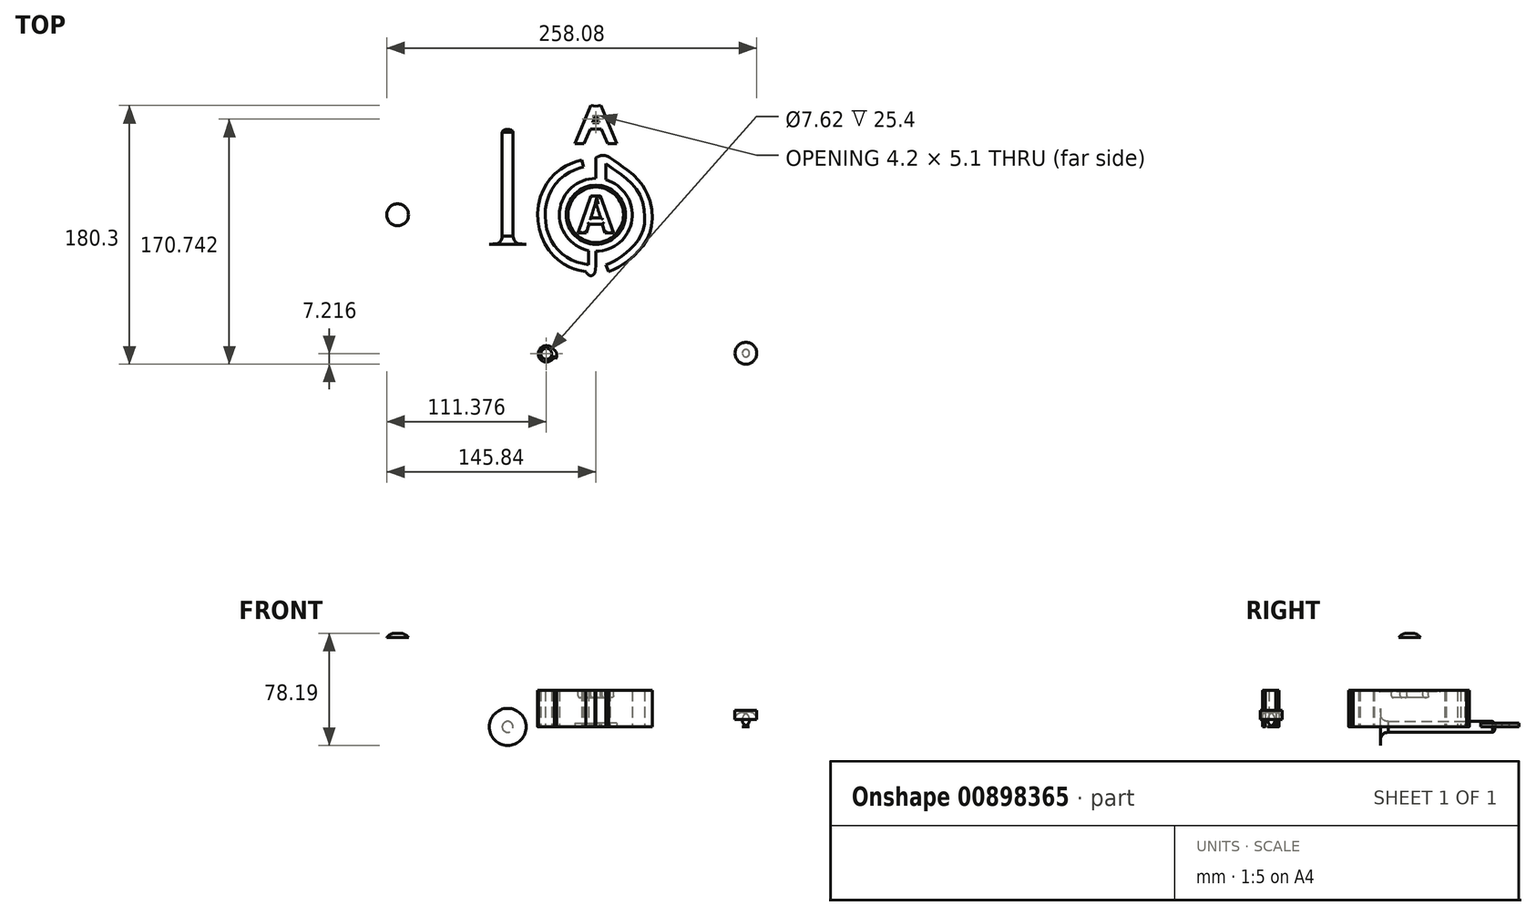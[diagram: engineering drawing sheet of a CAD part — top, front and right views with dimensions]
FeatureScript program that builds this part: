
annotation { "Feature Type Name" : "Feature", "Feature Type Description" : "" }
export const myFeature = defineFeature(function(context is Context, id is Id, definition is map)
    precondition{}
    {
        {
            var Q0;
            Q0=qCreatedBy(makeId("Top.planeOp"),FACE);
            var sketch = newSketch(context, id + "F0", { "sketchPlane" : qUnion([Q0])});
            skCircle(sketch, "E0", {"center": v(0, 0) * mm, "radius": 25.4 * mm});
            skLineSegment(sketch, "E1", {"start": v(0, 25.4) * mm, "end": v(0, 35.55) * mm});
            skLineSegment(sketch, "E2", {"start": v(0, -25.4) * mm, "end": v(0, -35.56) * mm});
            skFitSpline(sketch, "E3", {"points": [v(0, -35.56) * mm, v(-14.55, -32.5) * mm, v(-25.05, -25.72) * mm, v(-32.63, -14.55) * mm, v(-35.29, 2.2) * mm, v(-29.44, 19.74) * mm, v(-18, 29.84) * mm, v(-8.44, 33.43) * mm], "startDerivative": vector(-105, 14.53) * mm, "endDerivative": vector(78.17, 22.79) * mm});
            skFitSpline(sketch, "E4.0", {"points": [v(-0.7, -40.6) * mm, v(-1.8, -40.44) * mm, v(-4, -40.13) * mm, v(-7.4, -39.6) * mm, v(-10.23, -39.04) * mm, v(-12.5, -38.48) * mm, v(-14.2, -38) * mm, v(-15.6, -37.53) * mm, v(-16.7, -37.11) * mm, v(-18.35, -36.45) * mm, v(-20.72, -35.3) * mm, v(-23.66, -33.5) * mm, v(-25.92, -31.77) * mm, v(-27.63, -30.29) * mm, v(-29.26, -28.73) * mm, v(-31.2, -26.64) * mm, v(-33.34, -23.88) * mm, v(-35.25, -20.87) * mm, v(-36.9, -17.62) * mm, v(-38.28, -14.12) * mm, v(-39.34, -10.44) * mm, v(-40.07, -6.6) * mm, v(-40.46, -2.64) * mm, v(-40.48, 1.41) * mm, v(-40.11, 5.51) * mm, v(-39.35, 9.58) * mm, v(-38.2, 13.57) * mm, v(-36.65, 17.43) * mm, v(-35.2, 20.17) * mm, v(-34.1, 21.92) * mm, v(-33.32, 23.07) * mm, v(-31.9, 24.99) * mm, v(-29.68, 27.48) * mm, v(-26.83, 30.08) * mm, v(-24.35, 31.93) * mm, v(-22.35, 33.22) * mm, v(-20.85, 34.09) * mm, v(-19.36, 34.87) * mm, v(-17.4, 35.78) * mm, v(-15.04, 36.7) * mm, v(-12.36, 37.58) * mm, v(-10.68, 38.07) * mm, v(-9.86, 38.3) * mm]});
            skLineSegment(sketch, "E5", {"start": v(-0.7, -40.6) * mm, "end": v(0, -35.56) * mm});
            skLineSegment(sketch, "E6", {"start": v(-9.86, 38.3) * mm, "end": v(-8.44, 33.43) * mm});
            skLineSegment(sketch, "E7", {"start": v(-5.08, -34.86) * mm, "end": v(-5.08, -24.89) * mm});
            skFitSpline(sketch, "E8", {"points": [v(7.04, 35.55) * mm, v(14.69, 30.24) * mm, v(29.7, 15.62) * mm, v(33.56, -8.04) * mm, v(26.12, -21.73) * mm, v(14.42, -31.3) * mm, v(7.04, -34.76) * mm], "startDerivative": vector(51.9, -35.75) * mm, "endDerivative": vector(-56.85, -22.28) * mm});
            skFitSpline(sketch, "E9.0", {"points": [v(9.92, 39.74) * mm, v(10.46, 39.36) * mm, v(11.54, 38.62) * mm, v(13.24, 37.44) * mm, v(14.77, 36.38) * mm, v(16.1, 35.46) * mm, v(17.15, 34.72) * mm, v(18.26, 33.93) * mm, v(19.48, 33.07) * mm, v(20.76, 32.14) * mm, v(22.54, 30.8) * mm, v(24.86, 28.93) * mm, v(27.68, 26.37) * mm, v(29.97, 23.93) * mm, v(31.7, 21.78) * mm, v(32.73, 20.35) * mm, v(33.51, 19.15) * mm, v(34.07, 18.23) * mm, v(34.6, 17.27) * mm, v(35.27, 15.99) * mm, v(36.02, 14.34) * mm, v(37.06, 11.66) * mm, v(38.07, 8.22) * mm, v(38.85, 4.05) * mm, v(39.23, -0.1) * mm, v(39.2, -4.15) * mm, v(38.86, -7.4) * mm, v(38.38, -9.9) * mm, v(37.77, -12.29) * mm, v(36.76, -15.1) * mm, v(35.21, -18.17) * mm, v(33.4, -20.98) * mm, v(31.7, -23.1) * mm, v(30.28, -24.72) * mm, v(28.81, -26.28) * mm, v(26.88, -28.17) * mm, v(24.48, -30.3) * mm, v(22.02, -32.27) * mm, v(19.98, -33.75) * mm, v(18.37, -34.83) * mm, v(17.18, -35.58) * mm, v(16, -36.26) * mm, v(14.5, -37.07) * mm, v(12.7, -37.93) * mm, v(10.71, -38.77) * mm, v(9.48, -39.25) * mm, v(8.9, -39.49) * mm]});
            skLineSegment(sketch, "E10", {"start": v(0, 39.74) * mm, "end": v(0, 35.55) * mm});
            skLineSegment(sketch, "E11", {"start": v(7.04, 35.55) * mm, "end": v(7.04, 24.4) * mm});
            skLineSegment(sketch, "E12", {"start": v(7.04, -34.76) * mm, "end": v(8.9, -39.49) * mm});
            skFitSpline(sketch, "E13", {"points": [v(9.92, 39.74) * mm, v(6.86, 41.24) * mm, v(3.27, 41.24) * mm, v(0, 39.74) * mm], "startDerivative": vector(-8.92, 5.5) * mm, "endDerivative": vector(-9.37, -5.34) * mm});
            skPoint(sketch, "E14.endDerivative.orphan", {"position": v(6.86, 42.74) * mm});
            skPoint(sketch, "E14.startDerivative.orphan", {"position": v(8.4, 41.24) * mm});
            skPoint(sketch, "E15.1.internal.orphan", {"position": v(-2.62, -40.6) * mm});
            skFitSpline(sketch, "E16", {"points": [v(-0.7, -40.6) * mm, v(-2.62, -42.28) * mm, v(-4.27, -42.28) * mm, v(-6.26, -40.6) * mm, v(-7.03, -39.64) * mm], "startDerivative": vector(-6.65, -7.21) * mm, "endDerivative": vector(-3.2, 4.38) * mm});
            skPoint(sketch, "E17.orphan", {"position": v(4, 0) * mm});
            skPoint(sketch, "E18", {"position": v(0, -3.17) * mm});
            skPoint(sketch, "E19.start.orphan", {"position": v(-10.06, 0) * mm});
            skCircle(sketch, "E20", {"center": v(0, 0) * mm, "radius": 19.32 * mm});
            skCircle(sketch, "E21", {"center": v(0, 0) * mm, "radius": 20.67 * mm});
            skCircle(sketch, "E22", {"center": v(-34.46, -96.85) * mm, "radius": 3.81 * mm});
            skArc(sketch, "E23", {"start": v(-29.9, -93.5) * mm, "mid": v(-40.02, -98.01) * mm, "end": v(-28.93, -98.1) * mm});
            skLineSegment(sketch, "E24", {"start": v(-28.93, -98.1) * mm, "end": v(-27.97, -100.51) * mm});
            skArc(sketch, "E25", {"start": v(-27.97, -100.51) * mm, "mid": v(-27.37, -96.57) * mm, "end": v(-29.9, -93.5) * mm});
            skPoint(sketch, "E26.end.orphan", {"position": v(9.26, -7.36) * mm});
            skPoint(sketch, "E27.end.orphan", {"position": v(-17.78, -7.36) * mm});
            skPoint(sketch, "E27.start.orphan", {"position": v(0, 12.15) * mm});
            skPoint(sketch, "E28.start.orphan", {"position": v(0, 4.35) * mm});
            skPoint(sketch, "E29.start.orphan", {"position": v(-3.86, 0) * mm});
            skSolve(sketch);
        }
        {
            var Q0;
            Q0 = qSketchRegion(id + "F0", true);
            extrude(context, id + "F1", {"entities" : qUnion([Q0]), "depth" : 25.4 * mm, "offsetDistance" : 25.4 * mm});
        }
        {
            var Q0;
            Q0=qCreatedBy(makeId("Front.planeOp"),FACE);
            var sketch = newSketch(context, id + "F2", { "sketchPlane" : qUnion([Q0])});
            skLineSegment(sketch, "E30", {"start": v(-130.6, 62.22) * mm, "end": v(-138.22, 62.22) * mm});
            skFitSpline(sketch, "E31", {"points": [v(-130.6, 62.22) * mm, v(-131.95, 63.64) * mm, v(-133.54, 64.67) * mm, v(-135.8, 65.24) * mm, v(-138.22, 65.25) * mm], "startDerivative": vector(-4.63, 6.31) * mm, "endDerivative": vector(-8.46, -0.46) * mm});
            skLineSegment(sketch, "E32", {"start": v(-138.22, 65.25) * mm, "end": v(-138.22, 62.22) * mm});
            skSolve(sketch);
        }
        {
            var Q0;
            Q0=makeQuery(id+"F0.imprint","IMPRINT",FACE,{"disambiguationData":[TD([[makeQuery(id+"F0.imprint","IMPRINT",EDGE,{"derivedFrom":sQuery(id+"F0.wireOp",EDGE,"E20")}),-1.0]])]});
            var Q1;
            Q1=makeQuery(id+"F0.imprint","IMPRINT",FACE,{"disambiguationData":[TD([[makeQuery(id+"F0.imprint","IMPRINT",EDGE,{"derivedFrom":sQuery(id+"F0.wireOp",EDGE,"E28")}),-1.0]])]});
            extrude(context, id + "F3", {"entities" : qUnion([Q0, Q1]), "operationType" : NewBodyOperationType.ADD, "depth" : 24.9 * mm, "offsetDistance" : 25.4 * mm});
        }
        {
            var Q0;
            Q0=makeQuery(id+"F2.imprint","IMPRINT",FACE,{"disambiguationData":[TD([[makeQuery(id+"F2.imprint","IMPRINT",EDGE,{"derivedFrom":sQuery(id+"F2.wireOp",EDGE,"E30")}),-1.0]])]});
            var Q1;
            Q1=sQuery(id+"F2.wireOp",EDGE,"E32");
            revolve(context, id + "F4", {"surfaceOperationType" : NewSurfaceOperationType.NEW, "entities" : qUnion([Q0]), "axis" : qUnion([Q1]), "revolveType" : RevolveType.FULL});
        }
        {
            var Q0;
            Q0=qCreatedBy(makeId("Top.planeOp"),FACE);
            var sketch = newSketch(context, id + "F5", { "sketchPlane" : qUnion([Q0])});
            skLineSegment(sketch, "E33.top", {"start": v(-65.27, 27.3) * mm, "end": v(-61.46, 27.3) * mm});
            skLineSegment(sketch, "E33.left", {"start": v(-65.27, 57.66) * mm, "end": v(-65.27, 27.3) * mm});
            skLineSegment(sketch, "E33.right", {"start": v(-61.46, 57.66) * mm, "end": v(-61.46, 27.3) * mm});
            skFitSpline(sketch, "E34", {"points": [v(-65.27, 57.66) * mm, v(-64.7, 58.62) * mm, v(-63.78, 59.15) * mm, v(-62.33, 59.48) * mm, v(-61.46, 59.55) * mm], "startDerivative": vector(2.04, 4.24) * mm, "endDerivative": vector(3.67, 0.16) * mm});
            skLineSegment(sketch, "E35", {"start": v(-61.46, 59.55) * mm, "end": v(-61.46, 57.66) * mm});
            skLineSegment(sketch, "E36", {"start": v(-65.27, 27.3) * mm, "end": v(-65.27, 15.9) * mm});
            skLineSegment(sketch, "E37", {"start": v(-61.46, 27.3) * mm, "end": v(-61.46, 15.9) * mm});
            skLineSegment(sketch, "E38", {"start": v(-61.46, 15.9) * mm, "end": v(-65.27, 15.9) * mm});
            skLineSegment(sketch, "E39", {"start": v(-61.46, 15.9) * mm, "end": v(-61.46, -14.88) * mm});
            skLineSegment(sketch, "E40", {"start": v(-65.27, -14.88) * mm, "end": v(-65.27, 15.9) * mm});
            skFitSpline(sketch, "E41", {"points": [v(-65.27, -14.88) * mm, v(-65.92, -17.73) * mm, v(-68.2, -19.87) * mm, v(-71.2, -20.38) * mm, v(-74.37, -20.47) * mm], "startDerivative": vector(-1.14, -12.1) * mm, "endDerivative": vector(-12.5, -0.3) * mm});
            skLineSegment(sketch, "E42", {"start": v(-74.37, -20.47) * mm, "end": v(-61.46, -20.47) * mm});
            skLineSegment(sketch, "E43", {"start": v(-61.46, -20.47) * mm, "end": v(-61.46, -14.88) * mm});
            skSolve(sketch);
        }
        {
            var Q0;
            Q0 = qSketchRegion(id + "F5", true);
            var Q1;
            Q1=sQuery(id+"F5.wireOp",EDGE,"E33.right");
            revolve(context, id + "F6", {"surfaceOperationType" : NewSurfaceOperationType.NEW, "entities" : qUnion([Q0]), "axis" : qUnion([Q1]), "revolveType" : RevolveType.FULL});
        }
        {
            var Q0;
            Q0=qCreatedBy(makeId("Top.planeOp"),FACE);
            var sketch = newSketch(context, id + "F7", { "sketchPlane" : qUnion([Q0])});
            skCircle(sketch, "E44", {"center": v(104.62, -96.45) * mm, "radius": 7.62 * mm});
            skPoint(sketch, "E45.center.orphan", {"position": v(104.62, 20.59) * mm});
            skSolve(sketch);
        }
        {
            var Q0;
            Q0 = qSketchRegion(id + "F7", true);
            extrude(context, id + "F8", {"entities" : qUnion([Q0]), "depth" : 11.43 * mm, "offsetDistance" : 25.4 * mm});
        }
        {
            var Q0;
            Q0=makeQuery(id+"F8.opExtrude","CAP_EDGE",EDGE,{"disambiguationData":[OSD([sQuery(id+"F7.wireOp",EDGE,"E44")])],"isStart":true});
            fillet(context, id + "F9", {"entities" : qUnion([Q0]), "radius" : 5.08 * mm, "tangentPropagation" : true, "allowEdgeOverflow" : false});
        }
        {
            var Q0;
            Q0=makeQuery(id+"F0.imprint","IMPRINT",FACE,{"disambiguationData":[TD([[makeQuery(id+"F0.imprint","IMPRINT",EDGE,{"derivedFrom":sQuery(id+"F0.wireOp",EDGE,"E20")}),1.0]])]});
            extrude(context, id + "F10", {"entities" : qUnion([Q0]), "operationType" : NewBodyOperationType.ADD, "depth" : 25.4 * mm, "offsetDistance" : 25.4 * mm});
        }
        {
            var Q0;
            Q0=qCreatedBy(makeId("Top.planeOp"),FACE);
            var sketch = newSketch(context, id + "F11", { "sketchPlane" : qUnion([Q0])});
            skPoint(sketch, "E46.end.orphan", {"position": v(8947.36, -21346.4) * mm});
            skPoint(sketch, "E47.end.orphan", {"position": v(0, 75.75) * mm});
            skPoint(sketch, "E47.start.orphan", {"position": v(8930.06, -21346.4) * mm});
            skPoint(sketch, "E48.end.orphan", {"position": v(5.76, 75.75) * mm});
            skLineSegment(sketch, "E49", {"start": v(-14.52, 49.5) * mm, "end": v(-3.52, 76.23) * mm});
            skLineSegment(sketch, "E50", {"start": v(-14.52, 49.5) * mm, "end": v(-8.23, 49.5) * mm});
            skLineSegment(sketch, "E51", {"start": v(-8.23, 49.5) * mm, "end": v(-3.67, 59.88) * mm});
            skLineSegment(sketch, "E52", {"start": v(-3.67, 59.88) * mm, "end": v(0, 59.88) * mm});
            skLineSegment(sketch, "E53", {"start": v(-2.1, 64.12) * mm, "end": v(0, 69.22) * mm});
            skLineSegment(sketch, "E54", {"start": v(-2.1, 64.12) * mm, "end": v(0, 64.12) * mm});
            skLineSegment(sketch, "E55", {"start": v(-3.52, 76.23) * mm, "end": v(0, 75.75) * mm});
            skLineSegment(sketch, "E56.MirrorCS", {"start": v(14.52, 49.5) * mm, "end": v(3.52, 76.23) * mm});
            skLineSegment(sketch, "E57.MirrorCS", {"start": v(3.52, 76.23) * mm, "end": v(0, 75.75) * mm});
            skLineSegment(sketch, "E58.MirrorCS", {"start": v(2.1, 64.12) * mm, "end": v(0, 69.22) * mm});
            skLineSegment(sketch, "E59.MirrorCS", {"start": v(2.1, 64.12) * mm, "end": v(0, 64.12) * mm});
            skLineSegment(sketch, "E60.MirrorCS", {"start": v(3.67, 59.88) * mm, "end": v(0, 59.88) * mm});
            skLineSegment(sketch, "E61.MirrorCS", {"start": v(8.23, 49.5) * mm, "end": v(3.67, 59.88) * mm});
            skLineSegment(sketch, "E62.MirrorCS", {"start": v(14.52, 49.5) * mm, "end": v(8.23, 49.5) * mm});
            skSolve(sketch);
        }
        {
            var Q0;
            Q0 = qSketchRegion(id + "F11", true);
            extrude(context, id + "F12", {"entities" : qUnion([Q0]), "depth" : 2.54 * mm, "offsetDistance" : 25.4 * mm});
        }
        {
            var Q0;
            Q0=makeQuery(id+"F10.opExtrude","CAP_FACE",FACE,{"disambiguationData":[OSD([sQuery(id+"F0.wireOp",EDGE,"E20")])],"isStart":false});
            var sketch = newSketch(context, id + "F13", { "sketchPlane" : qUnion([Q0])});
            skText(sketch, "E63", { "text": "A", "fontName": "OpenSans-Bold.ttf"});
            const initialGuessF13  = {"E63": [-0.01248, -0.01265, 1, 0, 0.02583]};
            skSetInitialGuess(sketch, initialGuessF13);
            skSolve(sketch);
        }
        {
            var Q0;
            Q0=makeQuery(id+"F13.imprint","IMPRINT",FACE,{"disambiguationData":[TD([[makeQuery(id+"F13.imprint","IMPRINT",EDGE,{"derivedFrom":sQuery(id+"F13.wireOp",EDGE,"E63.sketch_text.stroke-0")}),-1.0]])]});
            extrude(context, id + "F14", {"entities" : qUnion([Q0]), "operationType" : NewBodyOperationType.REMOVE, "oppositeDirection" : true, "depth" : 5.08 * mm, "offsetDistance" : 25.4 * mm});
        }
        {
            var Q0;
            Q0=makeQuery(id+"F14.boolean.opBoolean","COPY",EDGE,{"derivedFrom":makeQuery(id+"F14.opExtrude","CAP_EDGE",EDGE,{"disambiguationData":[OSD([sQuery(id+"F13.wireOp",EDGE,"E63.sketch_text.stroke-8")])],"isStart":false})});
            var Q1;
            Q1=makeQuery(id+"F14.boolean.opBoolean","COPY",EDGE,{"derivedFrom":makeQuery(id+"F14.opExtrude","CAP_EDGE",EDGE,{"disambiguationData":[OSD([sQuery(id+"F13.wireOp",EDGE,"E63.sketch_text.stroke-6")])],"isStart":false})});
            var Q2;
            Q2=makeQuery(id+"F14.boolean.opBoolean","COPY",EDGE,{"derivedFrom":makeQuery(id+"F14.opExtrude","CAP_EDGE",EDGE,{"disambiguationData":[OSD([sQuery(id+"F13.wireOp",EDGE,"E63.sketch_text.stroke-5")])],"isStart":false})});
            var Q3;
            Q3=makeQuery(id+"F14.boolean.opBoolean","COPY",EDGE,{"derivedFrom":makeQuery(id+"F14.opExtrude","CAP_EDGE",EDGE,{"disambiguationData":[OSD([sQuery(id+"F13.wireOp",EDGE,"E63.sketch_text.stroke-4")])],"isStart":false})});
            var Q4;
            Q4=makeQuery(id+"F14.boolean.opBoolean","COPY",EDGE,{"derivedFrom":makeQuery(id+"F14.opExtrude","CAP_EDGE",EDGE,{"disambiguationData":[OSD([sQuery(id+"F13.wireOp",EDGE,"E63.sketch_text.stroke-11")])],"isStart":false})});
            var Q5;
            Q5=makeQuery(id+"F14.boolean.opBoolean","COPY",EDGE,{"derivedFrom":makeQuery(id+"F14.opExtrude","CAP_EDGE",EDGE,{"disambiguationData":[OSD([sQuery(id+"F13.wireOp",EDGE,"E63.sketch_text.stroke-1")])],"isStart":false})});
            var Q6;
            Q6=makeQuery(id+"F14.boolean.opBoolean","COPY",EDGE,{"derivedFrom":makeQuery(id+"F14.opExtrude","CAP_EDGE",EDGE,{"disambiguationData":[OSD([sQuery(id+"F13.wireOp",EDGE,"E63.sketch_text.stroke-9")])],"isStart":false})});
            var Q7;
            Q7=makeQuery(id+"F14.boolean.opBoolean","COPY",EDGE,{"derivedFrom":makeQuery(id+"F14.opExtrude","CAP_EDGE",EDGE,{"disambiguationData":[OSD([sQuery(id+"F13.wireOp",EDGE,"E63.sketch_text.stroke-2")])],"isStart":false})});
            var Q8;
            Q8=makeQuery(id+"F14.boolean.opBoolean","COPY",EDGE,{"derivedFrom":makeQuery(id+"F14.opExtrude","CAP_EDGE",EDGE,{"disambiguationData":[OSD([sQuery(id+"F13.wireOp",EDGE,"E63.sketch_text.stroke-3")])],"isStart":false})});
            var Q9;
            Q9=makeQuery(id+"F14.boolean.opBoolean","COPY",EDGE,{"derivedFrom":makeQuery(id+"F14.opExtrude","CAP_EDGE",EDGE,{"disambiguationData":[OSD([sQuery(id+"F13.wireOp",EDGE,"E63.sketch_text.stroke-0")])],"isStart":false})});
            var Q10;
            Q10=makeQuery(id+"F14.boolean.opBoolean","COPY",EDGE,{"derivedFrom":makeQuery(id+"F14.opExtrude","CAP_EDGE",EDGE,{"disambiguationData":[OSD([sQuery(id+"F13.wireOp",EDGE,"E63.sketch_text.stroke-7")])],"isStart":false})});
            fillet(context, id + "F15", {"entities" : qUnion([Q0, Q1, Q2, Q3, Q4, Q5, Q6, Q7, Q8, Q9, Q10]), "radius" : 1.27 * mm, "tangentPropagation" : true, "allowEdgeOverflow" : false});
        }
        {
            var Q0;
            Q0=makeQuery(id+"F10.opExtrude","CAP_EDGE",EDGE,{"disambiguationData":[OSD([sQuery(id+"F0.wireOp",EDGE,"E20")])],"isStart":false});
            fillet(context, id + "F16", {"entities" : qUnion([Q0]), "radius" : 1.27 * mm, "tangentPropagation" : true, "allowEdgeOverflow" : false});
        }
        {
            var Q0;
            Q0=makeQuery(id+"F1.opExtrude","CAP_EDGE",EDGE,{"disambiguationData":[OSD([sQuery(id+"F0.wireOp",EDGE,"E21")])],"isStart":false});
            fillet(context, id + "F17", {"entities" : qUnion([Q0]), "radius" : 1.27 * mm, "tangentPropagation" : true, "allowEdgeOverflow" : false});
        }
    });
